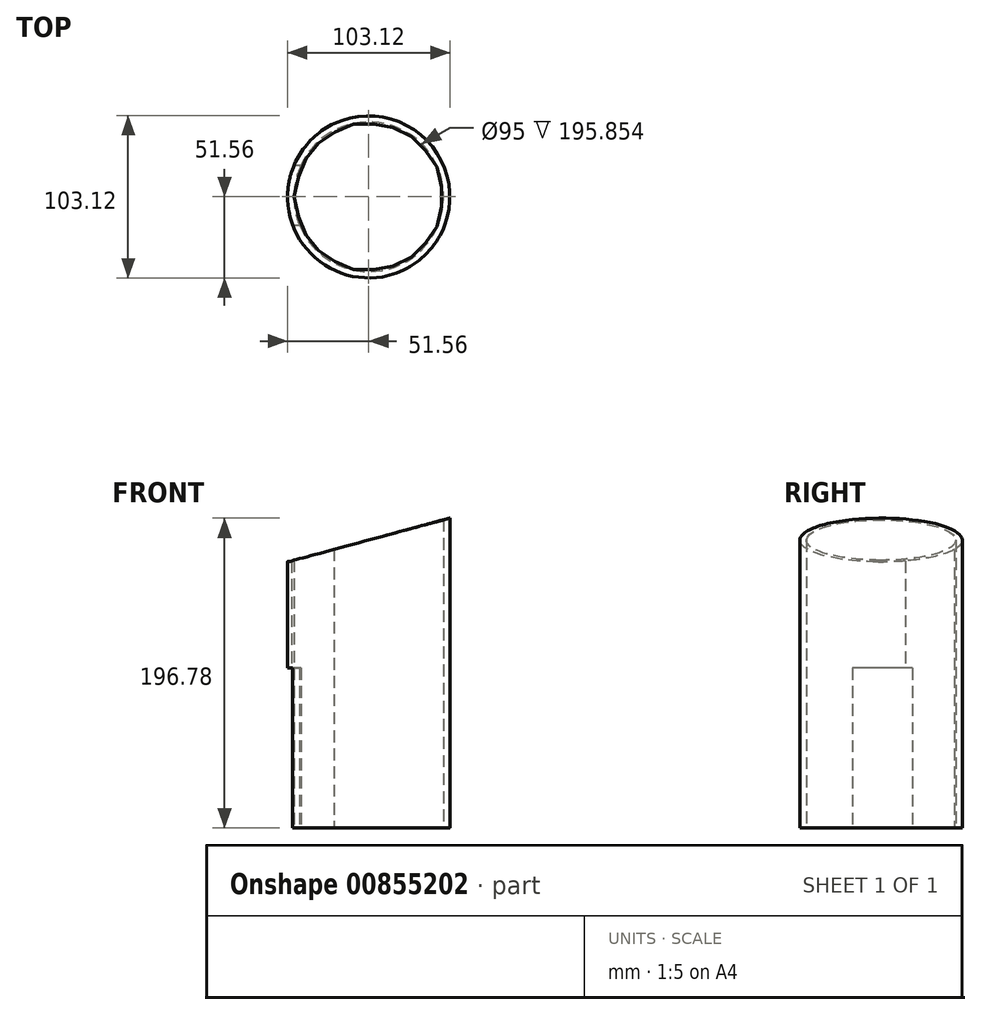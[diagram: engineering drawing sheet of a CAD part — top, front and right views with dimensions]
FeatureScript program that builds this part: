
annotation { "Feature Type Name" : "Feature", "Feature Type Description" : "" }
export const myFeature = defineFeature(function(context is Context, id is Id, definition is map)
    precondition{}
    {
        {
            var Q0;
            Q0=qCreatedBy(makeId("Top.planeOp"),FACE);
            var sketch = newSketch(context, id + "F0", { "sketchPlane" : qUnion([Q0])});
            skCircle(sketch, "E0", {"center": v(0, 0) * mm, "radius": 51.56 * mm});
            skCircle(sketch, "E1", {"center": v(0, 0) * mm, "radius": 47.5 * mm});
            skSolve(sketch);
        }
        {
            var Q0;
            Q0=qSketchRegion(id+"F0",true);
            extrude(context, id + "F1", {"entities" : qUnion([Q0]), "depth" : 196.85 * mm, "offsetDistance" : 25 * mm});
        }
        {
            var Q0;
            Q0=qCreatedBy(makeId("Front.planeOp"),FACE);
            var sketch = newSketch(context, id + "F2", { "sketchPlane" : qUnion([Q0])});
            skLineSegment(sketch, "E2", {"start": v(-56.99, 0) * mm, "end": v(-56.99, 168.91) * mm, "construction": true});
            skLineSegment(sketch, "E3", {"start": v(-51.54, 168.91) * mm, "end": v(53.58, 197.32) * mm});
            skLineSegment(sketch, "E4", {"start": v(53.58, 197.32) * mm, "end": v(-53.91, 197.32) * mm});
            skLineSegment(sketch, "E5", {"start": v(-53.91, 197.32) * mm, "end": v(-51.54, 168.91) * mm});
            skSolve(sketch);
        }
        {
            var Q0;
            Q0=qSketchRegion(id+"F2",true);
            extrude(context, id + "F3", {"entities" : qUnion([Q0]), "operationType" : NewBodyOperationType.REMOVE, "depth" : 61 * mm, "offsetDistance" : 25 * mm, "hasSecondDirection" : true, "secondDirectionOppositeDirection" : true, "secondDirectionDepth" : 74 * mm});
        }
        {
            var Q0;
            Q0=qCreatedBy(makeId("Right.planeOp"),FACE);
            var sketch = newSketch(context, id + "F4", { "sketchPlane" : qUnion([Q0])});
            skLineSegment(sketch, "E6.bottom", {"start": v(20.02, 101.6) * mm, "end": v(-18.08, 101.6) * mm});
            skLineSegment(sketch, "E6.top", {"start": v(20.02, 0) * mm, "end": v(-18.08, 0) * mm});
            skLineSegment(sketch, "E6.left", {"start": v(20.02, 101.6) * mm, "end": v(20.02, 0) * mm});
            skLineSegment(sketch, "E6.right", {"start": v(-18.08, 101.6) * mm, "end": v(-18.08, 0) * mm});
            skSolve(sketch);
        }
        {
            var Q0;
            Q0=qSketchRegion(id+"F4",true);
            extrude(context, id + "F5", {"entities" : qUnion([Q0]), "operationType" : NewBodyOperationType.REMOVE, "oppositeDirection" : true, "depth" : 61 * mm, "offsetDistance" : 25 * mm});
        }
        {
            var Q0;
            Q0=qCreatedBy(makeId("Top.planeOp"),FACE);
            var sketch = newSketch(context, id + "F6", { "sketchPlane" : qUnion([Q0])});
            skArc(sketch, "E7", {"start": v(0, 51.9) * mm, "mid": v(-36.37, 36.4) * mm, "end": v(-51.78, 0) * mm});
            skArc(sketch, "E8", {"start": v(51.78, 0) * mm, "mid": v(36.45, 36.49) * mm, "end": v(0, 51.9) * mm});
            skArc(sketch, "E9", {"start": v(0, -51.65) * mm, "mid": v(36.4, -36.36) * mm, "end": v(51.78, 0) * mm});
            skArc(sketch, "E10", {"start": v(-51.78, 0) * mm, "mid": v(-36.49, -36.45) * mm, "end": v(0, -51.65) * mm});
            skLineSegment(sketch, "E11", {"start": v(-51.78, 0) * mm, "end": v(-55.26, 0) * mm});
            skLineSegment(sketch, "E12", {"start": v(-55.26, 0) * mm, "end": v(-55.26, 55.12) * mm});
            skLineSegment(sketch, "E13", {"start": v(-55.26, 55.12) * mm, "end": v(54.05, 51.9) * mm});
            skLineSegment(sketch, "E14", {"start": v(54.05, 51.9) * mm, "end": v(54.05, -56.1) * mm});
            skLineSegment(sketch, "E15", {"start": v(54.05, -56.1) * mm, "end": v(-55.26, -56.1) * mm});
            skLineSegment(sketch, "E16", {"start": v(-55.26, -56.1) * mm, "end": v(-55.26, 0) * mm});
            skSolve(sketch);
        }
        {
            var Q0;
            Q0=makeQuery(id+"F6.imprint","IMPRINT",FACE,{"disambiguationData":[TD([[makeQuery(id+"F6.imprint","IMPRINT",EDGE,{"derivedFrom":sQuery(id+"F6.wireOp",EDGE,"E7")}),-1.0]])]});
            extrude(context, id + "F7", {"entities" : qUnion([Q0]), "operationType" : NewBodyOperationType.REMOVE, "depth" : 222 * mm, "offsetDistance" : 25 * mm});
        }
    });
